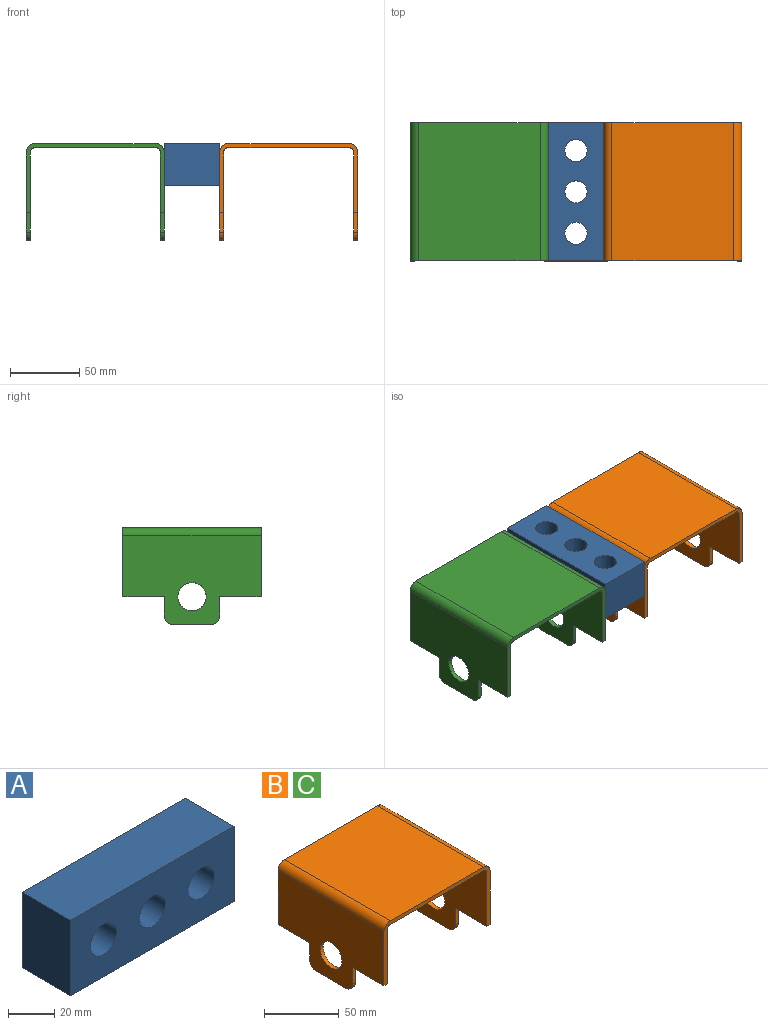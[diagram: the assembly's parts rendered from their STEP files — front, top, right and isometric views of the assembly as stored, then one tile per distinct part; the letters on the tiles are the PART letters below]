
ASSEMBLY  parts=3 mates=2
PART A: 9 faces, bbox 100x30x40 mm
  f0: plane 40x30mm, normal (-1,0,0), area 1200mm2, adj f1,f6,f7,f8
  f1: plane 100x30mm, normal (0,0,-1), area 3000mm2, adj f0,f2,f7,f8
  f2: plane 40x30mm, normal (1,0,0), area 1200mm2, adj f1,f6,f7,f8
  f3: cylinder r=8mm len=30mm, axis (0,1,0), area 1508mm2, adj f7,f8
  f4: cylinder r=8mm len=30mm, axis (0,1,0), area 1508mm2, adj f7,f8
  f5: cylinder r=8mm len=30mm, axis (0,1,0), area 1508mm2, adj f7,f8
  f6: plane 100x30mm, normal (0,0,1), area 3000mm2, adj f0,f2,f7,f8
  f7: plane 100x40mm, normal (0,-1,0), area 3396.8mm2, adj f0,f1,f2,f3,f4,f5,f6
  f8: plane 100x40mm, normal (0,1,0), area 3396.8mm2, adj f0,f1,f2,f3,f4,f5,f6
PART B: 28 faces, bbox 100x100x70 mm
  f0: plane 30x3mm, normal (0,0,-1), area 90mm2, adj f5,f7,f15,f22
  f1: plane 30x3mm, normal (0,0,-1), area 90mm2, adj f2,f11,f15,f17
  f2: plane 100x64mm, normal (1,0,0), area 4854.5mm2, adj f1,f12,f13,f14,f15,f16,f17,f18
  f3: plane 100x88mm, normal (0,0,-1), area 8800mm2, adj f4,f13,f14,f15
  f4: cylinder r=3mm len=100mm, axis (0,1,0), area 471.2mm2, adj f3,f5,f14,f15
  f5: plane 100x64mm, normal (-1,0,0), area 4854.5mm2, adj f0,f4,f6,f14,f15,f22,f23,f24
  f6: plane 30x3mm, normal (0,0,-1), area 90mm2, adj f5,f7,f14,f23
  f7: plane 100x64mm, normal (1,0,0), area 4854.5mm2, adj f0,f6,f8,f14,f15,f22,f23,f24
  f8: cylinder r=6mm len=100mm, axis (0,1,0), area 942.5mm2, adj f7,f9,f14,f15
  f9: plane 100x88mm, normal (0,0,1), area 8800mm2, adj f8,f10,f14,f15
  f10: cylinder r=6mm len=100mm, axis (0,1,0), area 942.5mm2, adj f9,f11,f14,f15
  f11: plane 100x64mm, normal (-1,0,0), area 4854.5mm2, adj f1,f10,f12,f14,f15,f16,f17,f18
  f12: plane 30x3mm, normal (0,0,-1), area 90mm2, adj f2,f11,f14,f21
  f13: cylinder r=3mm len=100mm, axis (0,1,0), area 471.2mm2, adj f2,f3,f14,f15
  f14: plane 100x50mm, normal (0,-1,0), area 570.4mm2, adj f2,f3,f4,f5,f6,f7,f8,f9
  f15: plane 100x50mm, normal (0,1,0), area 570.4mm2, adj f0,f1,f2,f3,f4,f5,f7,f8
  f16: cylinder r=10.25mm len=20.5mm, axis (-1,0,0), area 193.2mm2, adj f2,f11
  f17: plane 14x3mm, normal (0,1,0), area 42mm2, adj f1,f2,f11,f18
  f18: cylinder r=6mm len=6mm, axis (-1,0,0), area 28.3mm2, adj f2,f11,f17,f19
  f19: plane 28x3mm, normal (0,0,-1), area 84mm2, adj f2,f11,f18,f20
  f20: cylinder r=6mm len=6mm, axis (-1,0,0), area 28.3mm2, adj f2,f11,f19,f21
  f21: plane 14x3mm, normal (0,-1,0), area 42mm2, adj f2,f11,f12,f20
  f22: plane 14x3mm, normal (0,1,0), area 42mm2, adj f0,f5,f7,f26
  f23: plane 14x3mm, normal (0,-1,0), area 42mm2, adj f5,f6,f7,f24
  f24: cylinder r=6mm len=6mm, axis (1,0,0), area 28.3mm2, adj f5,f7,f23,f25
  f25: plane 28x3mm, normal (0,0,-1), area 84mm2, adj f5,f7,f24,f26
  f26: cylinder r=6mm len=6mm, axis (1,0,0), area 28.3mm2, adj f5,f7,f22,f25
  f27: cylinder r=10.25mm len=20.5mm, axis (1,0,0), area 193.2mm2, adj f5,f7
PART C: same geometry as B
PLACE A rot(axis=(0.58,0.58,0.58),120deg) t=(-3.52,-55.19,55.19)mm
PLACE B t=(66.48,-5.19,31.34)mm
PLACE C rot(axis=(0,0,-1),180deg) t=(-73.52,-105.19,31.34)mm
MATE parallel C.f9 <-> B.f9  axis (0,0,1) through (-73.52,-55.19,55.19)mm
MATE parallel A.f6 <-> B.f11  axis (1,0,0) through (16.48,-55.19,40.19)mm
